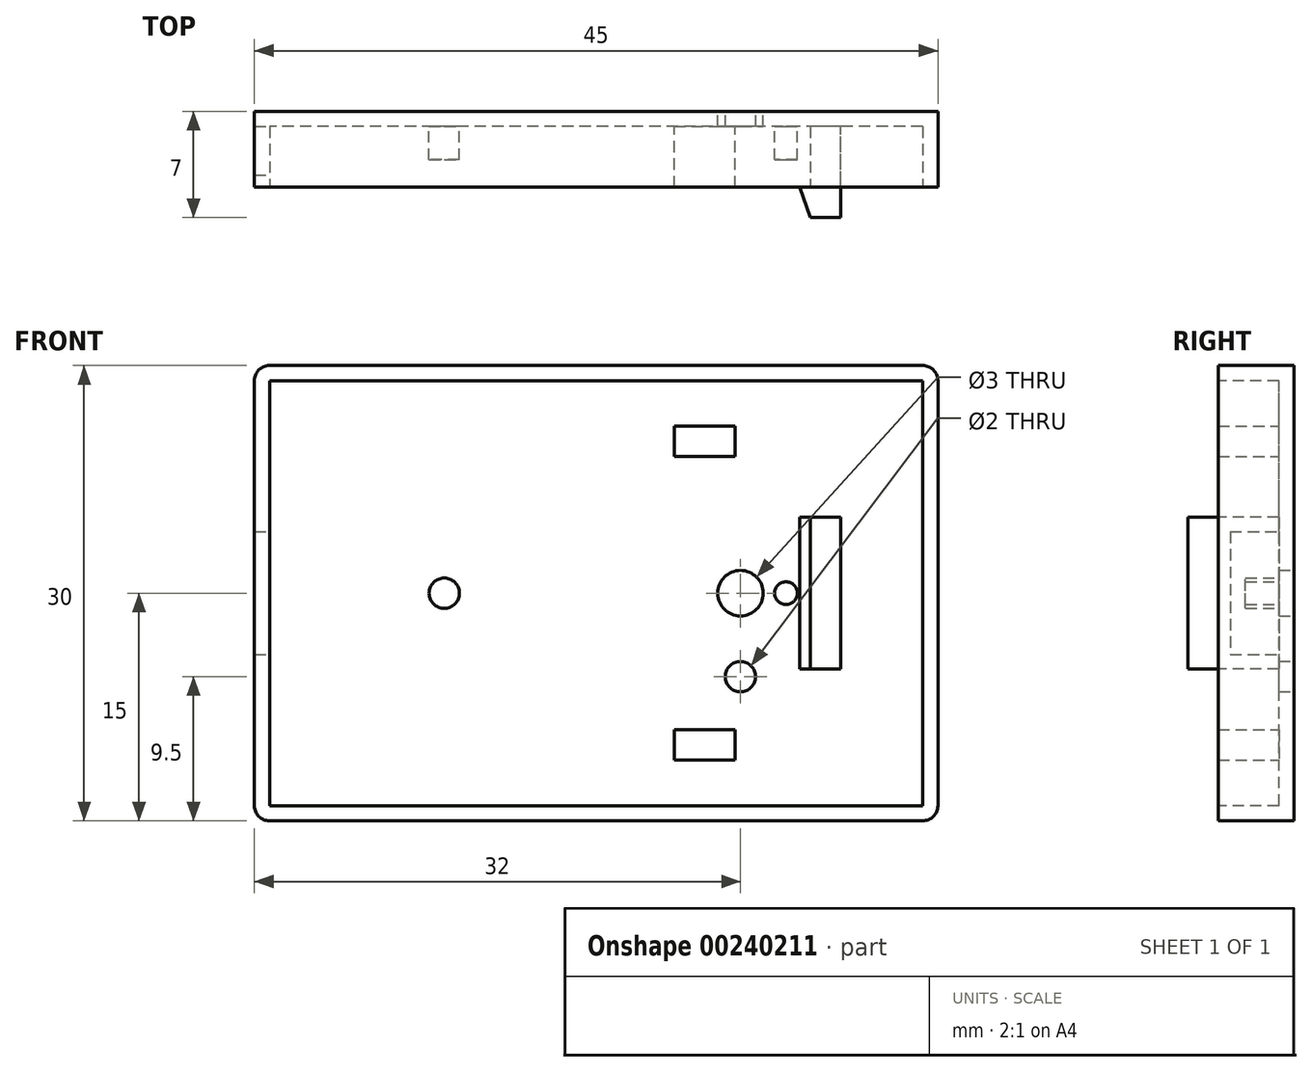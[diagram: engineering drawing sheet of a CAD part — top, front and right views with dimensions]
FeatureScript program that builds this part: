
annotation { "Feature Type Name" : "Feature", "Feature Type Description" : "" }
export const myFeature = defineFeature(function(context is Context, id is Id, definition is map)
    precondition{}
    {
        {
            var Q0;
            Q0=qCreatedBy(makeId("Front.planeOp"),FACE);
            var sketch = newSketch(context, id + "F0", { "sketchPlane" : qUnion([Q0])});
            skLineSegment(sketch, "E0.bottom", {"start": v(22.5, -15) * mm, "end": v(-22.5, -15) * mm});
            skLineSegment(sketch, "E0.top", {"start": v(22.5, 15) * mm, "end": v(-22.5, 15) * mm});
            skLineSegment(sketch, "E0.left", {"start": v(22.5, -15) * mm, "end": v(22.5, 15) * mm});
            skLineSegment(sketch, "E0.right", {"start": v(-22.5, -15) * mm, "end": v(-22.5, 15) * mm});
            skPoint(sketch, "E0.middle", {"position": v(0, 0) * mm});
            skCircle(sketch, "E1", {"center": v(-10, 0) * mm, "radius": 1 * mm});
            skCircle(sketch, "E2", {"center": v(9.5, 0) * mm, "radius": 1.5 * mm});
            skCircle(sketch, "E3", {"center": v(9.5, -5.5) * mm, "radius": 1 * mm});
            skSolve(sketch);
        }
        {
            var Q0;
            Q0=makeQuery(id+"F0.imprint","IMPRINT",FACE,{"disambiguationData":[TD([[makeQuery(id+"F0.imprint","IMPRINT",EDGE,{"derivedFrom":sQuery(id+"F0.wireOp",EDGE,"E0.bottom")}),-1.0]])]});
            var Q1;
            Q1=makeQuery(id+"F0.imprint","IMPRINT",FACE,{"disambiguationData":[TD([[makeQuery(id+"F0.imprint","IMPRINT",EDGE,{"derivedFrom":sQuery(id+"F0.wireOp",EDGE,"E1")}),1.0]])]});
            extrude(context, id + "F1", {"entities" : qUnion([Q0, Q1]), "depth" : 5 * mm});
        }
        {
            var Q0;
            Q0=makeQuery(id+"F1.opExtrude","SWEPT_EDGE",EDGE,{"disambiguationData":[OSD([sQuery(id+"F0.wireOp",EDGE,"E0.bottom"),sQuery(id+"F0.wireOp",EDGE,"E0.right")])]});
            var Q1;
            Q1=makeQuery(id+"F1.opExtrude","SWEPT_EDGE",EDGE,{"disambiguationData":[OSD([sQuery(id+"F0.wireOp",EDGE,"E0.bottom"),sQuery(id+"F0.wireOp",EDGE,"E0.left")])]});
            var Q2;
            Q2=makeQuery(id+"F1.opExtrude","SWEPT_EDGE",EDGE,{"disambiguationData":[OSD([sQuery(id+"F0.wireOp",EDGE,"E0.top"),sQuery(id+"F0.wireOp",EDGE,"E0.left")])]});
            var Q3;
            Q3=makeQuery(id+"F1.opExtrude","SWEPT_EDGE",EDGE,{"disambiguationData":[OSD([sQuery(id+"F0.wireOp",EDGE,"E0.top"),sQuery(id+"F0.wireOp",EDGE,"E0.right")])]});
            fillet(context, id + "F2", {"entities" : qUnion([Q0, Q1, Q2, Q3]), "radius" : 1 * mm, "tangentPropagation" : true, "allowEdgeOverflow" : false});
        }
        {
            var Q0;
            Q0=makeQuery(id+"F1.opExtrude","CAP_FACE",FACE,{"disambiguationData":[OSD([sQuery(id+"F0.wireOp",EDGE,"E0.bottom"),sQuery(id+"F0.wireOp",EDGE,"E0.top"),sQuery(id+"F0.wireOp",EDGE,"E0.left"),sQuery(id+"F0.wireOp",EDGE,"E0.right"),sQuery(id+"F0.wireOp",EDGE,"E2"),sQuery(id+"F0.wireOp",EDGE,"E3")])],"isStart":false});
            var Q1;
            Q1=makeQuery(id+"F1.opExtrude","SWEPT_FACE",FACE,{"disambiguationData":[OSD([sQuery(id+"F0.wireOp",EDGE,"E2")])]});
            var Q2;
            Q2=makeQuery(id+"F1.opExtrude","SWEPT_FACE",FACE,{"disambiguationData":[OSD([sQuery(id+"F0.wireOp",EDGE,"E3")])]});
            shell(context, id + "F3", {"entities" : qUnion([Q0, Q1, Q2]), "thickness" : 1 * mm});
        }
        {
            var Q0;
            Q0=makeQuery(id+"F3.opShell","OFFSET_FACE",FACE,{"disambiguationData":[OSD([sQuery(id+"F0.wireOp",EDGE,"E0.right")])]});
            var sketch = newSketch(context, id + "F4", { "sketchPlane" : qUnion([Q0])});
            skLineSegment(sketch, "E4.bottom", {"start": v(-1, -4.05) * mm, "end": v(-4.2, -4.05) * mm});
            skLineSegment(sketch, "E4.top", {"start": v(-1, 4.05) * mm, "end": v(-4.2, 4.05) * mm});
            skLineSegment(sketch, "E4.left", {"start": v(-1, -4.05) * mm, "end": v(-1, 4.05) * mm});
            skLineSegment(sketch, "E4.right", {"start": v(-4.2, -4.05) * mm, "end": v(-4.2, 4.05) * mm});
            skPoint(sketch, "E4.middle", {"position": v(-2.6, 0) * mm});
            skSolve(sketch);
        }
        {
            var Q0;
            Q0=makeQuery(id+"F4.imprint","IMPRINT",FACE,{"disambiguationData":[TD([[makeQuery(id+"F4.imprint","IMPRINT",EDGE,{"derivedFrom":sQuery(id+"F4.wireOp",EDGE,"E4.bottom")}),-1.0]])]});
            extrude(context, id + "F5", {"entities" : qUnion([Q0]), "operationType" : NewBodyOperationType.REMOVE, "oppositeDirection" : true, "depth" : 25 * mm});
        }
        {
            var Q0;
            Q0=makeQuery(id+"F3.opShell","OFFSET_FACE",FACE,{"disambiguationData":[OSD([sQuery(id+"F0.wireOp",EDGE,"E0.bottom"),sQuery(id+"F0.wireOp",EDGE,"E0.top"),sQuery(id+"F0.wireOp",EDGE,"E0.left"),sQuery(id+"F0.wireOp",EDGE,"E0.right"),sQuery(id+"F0.wireOp",EDGE,"E2"),sQuery(id+"F0.wireOp",EDGE,"E3")])]});
            var sketch = newSketch(context, id + "F6", { "sketchPlane" : qUnion([Q0])});
            skCircle(sketch, "E5", {"center": v(-10, 0) * mm, "radius": 1 * mm});
            skSolve(sketch);
        }
        {
            var Q0;
            Q0=makeQuery(id+"F6.imprint","IMPRINT",FACE,{"disambiguationData":[TD([[makeQuery(id+"F6.imprint","IMPRINT",EDGE,{"derivedFrom":sQuery(id+"F6.wireOp",EDGE,"E5")}),1.0]])]});
            extrude(context, id + "F7", {"entities" : qUnion([Q0]), "operationType" : NewBodyOperationType.ADD, "depth" : 2.2 * mm});
        }
        {
            var Q0;
            Q0=makeQuery(id+"F3.opShell","OFFSET_FACE",FACE,{"disambiguationData":[OSD([sQuery(id+"F0.wireOp",EDGE,"E0.right")])]});
            cPlane(context, id + "F8", {"entities" : qUnion([Q0]), "cplaneType" : CPlaneType.OFFSET, "offset" : 35.6 * mm, "width" : 150 * mm, "height" : 150 * mm});
        }
        {
            var Q0;
            Q0=qCreatedBy(makeId("Top.planeOp"),FACE);
            var sketch = newSketch(context, id + "F9", { "sketchPlane" : qUnion([Q0])});
            skLineSegment(sketch, "E6", {"start": v(14.1, 0) * mm, "end": v(14.1, -5) * mm});
            skLineSegment(sketch, "E7", {"start": v(14.1, -5) * mm, "end": v(13.4, -5) * mm});
            skLineSegment(sketch, "E8", {"start": v(13.4, -5) * mm, "end": v(14.1, -7) * mm});
            skLineSegment(sketch, "E9", {"start": v(14.1, -7) * mm, "end": v(16.1, -7) * mm});
            skLineSegment(sketch, "E10", {"start": v(16.1, -7) * mm, "end": v(16.1, 0) * mm});
            skLineSegment(sketch, "E11", {"start": v(16.1, 0) * mm, "end": v(14.1, 0) * mm});
            skSolve(sketch);
        }
        {
            var Q0;
            Q0=makeQuery(id+"F9.imprint","IMPRINT",FACE,{"disambiguationData":[TD([[makeQuery(id+"F9.imprint","IMPRINT",EDGE,{"derivedFrom":sQuery(id+"F9.wireOp",EDGE,"E6")}),1.0]])]});
            extrude(context, id + "F10", {"entities" : qUnion([Q0]), "operationType" : NewBodyOperationType.ADD, "endBound" : BoundingType.SYMMETRIC, "depth" : 10 * mm});
        }
        {
            var Q0;
            Q0=makeQuery(id+"F6.imprint","IMPRINT",FACE,{"disambiguationData":[TD([[makeQuery(id+"F6.imprint","IMPRINT",EDGE,{"derivedFrom":sQuery(id+"F6.wireOp",EDGE,"E5")}),-1.0]])]});
            var sketch = newSketch(context, id + "F11", { "sketchPlane" : qUnion([Q0])});
            skCircle(sketch, "E12", {"center": v(12.5, 0) * mm, "radius": 0.75 * mm});
            skSolve(sketch);
        }
        {
            var Q0;
            Q0=qSketchRegion(id+"F11",true);
            var Q1;
            Q1=makeQuery(id+"F7.opExtrude","CAP_FACE",FACE,{"disambiguationData":[OSD([sQuery(id+"F6.wireOp",EDGE,"E5")])],"isStart":false});
            extrude(context, id + "F12", {"entities" : qUnion([Q0]), "operationType" : NewBodyOperationType.ADD, "endBound" : BoundingType.UP_TO_SURFACE, "endBoundEntityFace" : qUnion([Q1]), "depth" : 25 * mm});
        }
        {
            var Q0;
            Q0=makeQuery(id+"F6.imprint","IMPRINT",FACE,{"disambiguationData":[TD([[makeQuery(id+"F6.imprint","IMPRINT",EDGE,{"derivedFrom":sQuery(id+"F6.wireOp",EDGE,"E5")}),-1.0]])]});
            var sketch = newSketch(context, id + "F13", { "sketchPlane" : qUnion([Q0])});
            skLineSegment(sketch, "E13.bottom", {"start": v(5.14, 9) * mm, "end": v(9.14, 9) * mm});
            skLineSegment(sketch, "E13.top", {"start": v(5.14, 11) * mm, "end": v(9.14, 11) * mm});
            skLineSegment(sketch, "E13.left", {"start": v(5.14, 9) * mm, "end": v(5.14, 11) * mm});
            skLineSegment(sketch, "E13.right", {"start": v(9.14, 9) * mm, "end": v(9.14, 11) * mm});
            skLineSegment(sketch, "E14.bottom", {"start": v(9.14, -9) * mm, "end": v(5.14, -9) * mm});
            skLineSegment(sketch, "E14.top", {"start": v(9.14, -11) * mm, "end": v(5.14, -11) * mm});
            skLineSegment(sketch, "E14.left", {"start": v(9.14, -9) * mm, "end": v(9.14, -11) * mm});
            skLineSegment(sketch, "E14.right", {"start": v(5.14, -9) * mm, "end": v(5.14, -11) * mm});
            skSolve(sketch);
        }
        {
            var Q0;
            Q0=qSketchRegion(id+"F13",true);
            var Q1;
            Q1=makeQuery(id+"F10.opExtrude","SWEPT_FACE",FACE,{"disambiguationData":[OSD([sQuery(id+"F9.wireOp",EDGE,"E7")])]});
            extrude(context, id + "F14", {"entities" : qUnion([Q0]), "operationType" : NewBodyOperationType.ADD, "endBound" : BoundingType.UP_TO_SURFACE, "endBoundEntityFace" : qUnion([Q1]), "depth" : 25 * mm});
        }
    });
